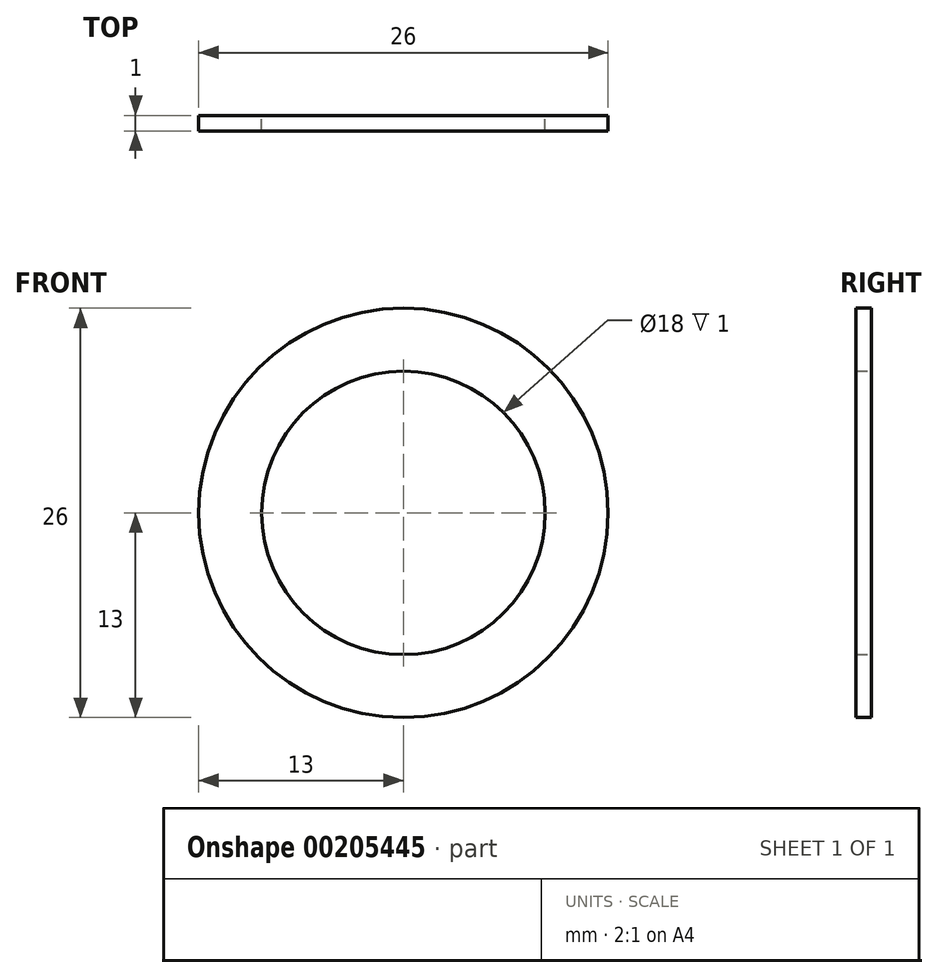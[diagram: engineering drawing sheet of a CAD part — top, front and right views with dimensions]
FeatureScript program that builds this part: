
annotation { "Feature Type Name" : "Feature", "Feature Type Description" : "" }
export const myFeature = defineFeature(function(context is Context, id is Id, definition is map)
    precondition{}
    {
        {
            var Q0;
            Q0=qCreatedBy(makeId("Front.planeOp"),FACE);
            var sketch = newSketch(context, id + "F0", { "sketchPlane" : qUnion([Q0])});
            skCircle(sketch, "E0", {"center": v(0, 0) * mm, "radius": 13 * mm});
            skCircle(sketch, "E1", {"center": v(0, 0) * mm, "radius": 9 * mm});
            skSolve(sketch);
        }
        {
            var Q0;
            Q0=makeQuery(id+"F0.imprint","IMPRINT",FACE,{"disambiguationData":[TD([[makeQuery(id+"F0.imprint","IMPRINT",EDGE,{"derivedFrom":sQuery(id+"F0.wireOp",EDGE,"E0")}),1.0]])]});
            extrude(context, id + "F1", {"entities" : qUnion([Q0]), "depth" : 1 * mm});
        }
    });
